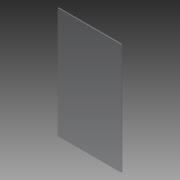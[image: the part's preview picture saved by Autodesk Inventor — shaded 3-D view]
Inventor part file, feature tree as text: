
AUTODESK INVENTOR PART (.ipt)
format: ipt  version: 2014 (Build 180170000, 170)  size: 69,120 bytes
history: native  units: in
note: dims shown in document units (in); Inventor stores cm internally (conversion verified against a paired STEP export)
features: extrude x1, sketch x1
ambient origin geometry x8: Origin, YZ Plane, XZ Plane, XY Plane, X Axis, Y Axis, Z Axis, Center Point
bodies: Solid1 (feature_tree)
feature tree (2):
  extrude  "Extrusion1"  Depth=14.0in
  sketch  "Sketch1"  dims[d0=8.0in d1=14.0in d2=0.125in d3=0.0in]
